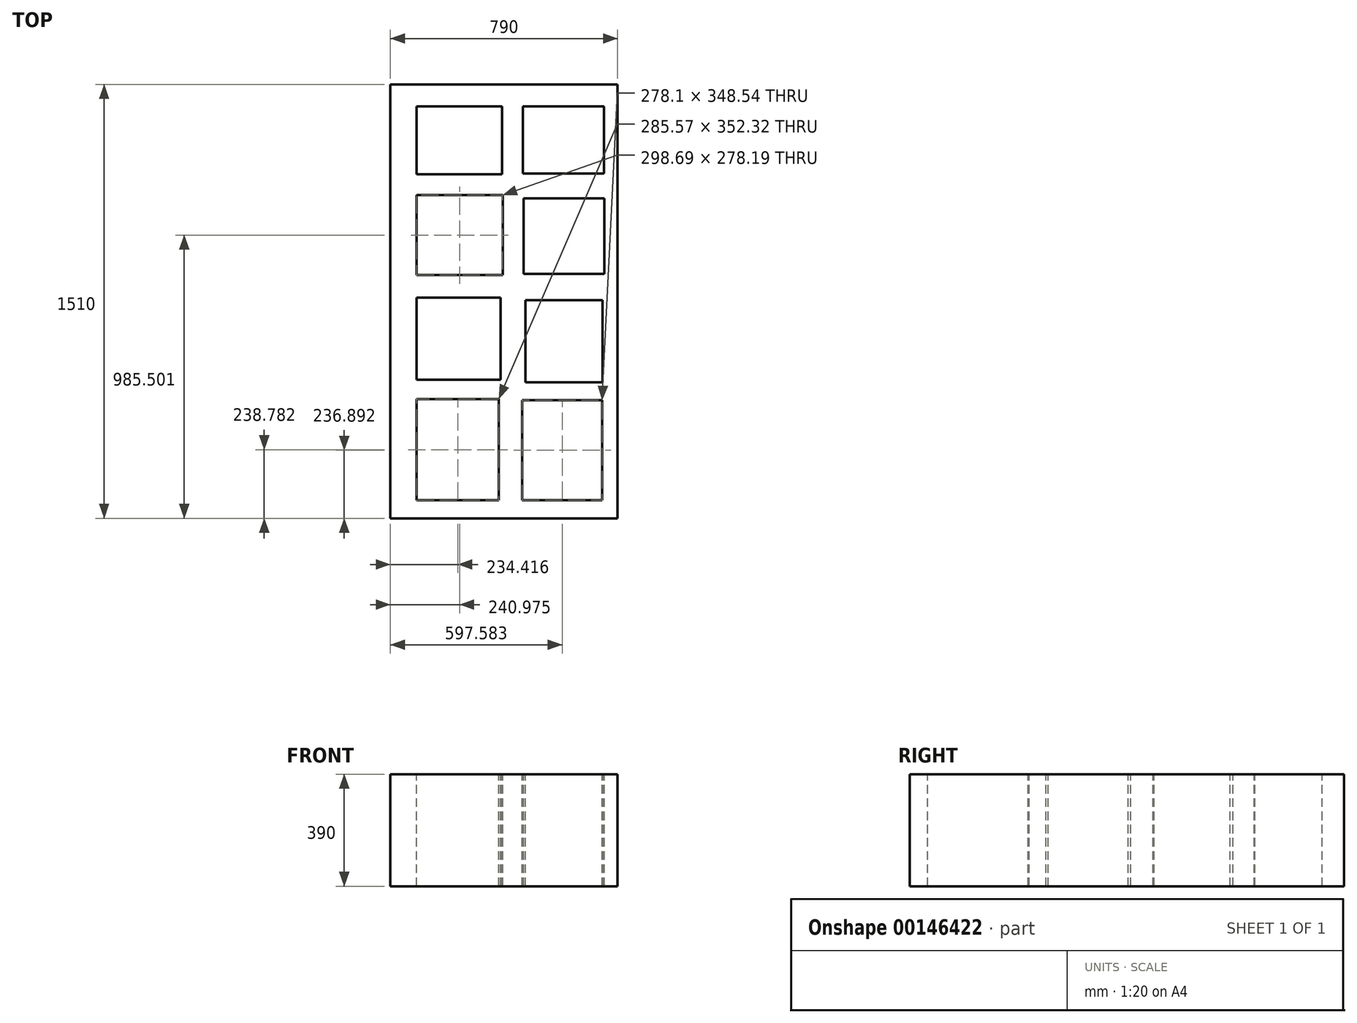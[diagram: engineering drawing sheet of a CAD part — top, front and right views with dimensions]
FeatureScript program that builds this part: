
annotation { "Feature Type Name" : "Feature", "Feature Type Description" : "" }
export const myFeature = defineFeature(function(context is Context, id is Id, definition is map)
    precondition{}
    {
        {
            var Q0;
            Q0=qCreatedBy(makeId("Top.planeOp"),FACE);
            var sketch = newSketch(context, id + "F0", { "sketchPlane" : qUnion([Q0])});
            skLineSegment(sketch, "E0.bottom", {"start": v(-91.63, -62.62) * mm, "end": v(698.37, -62.62) * mm});
            skLineSegment(sketch, "E0.top", {"start": v(-91.63, 1447.38) * mm, "end": v(698.37, 1447.38) * mm});
            skLineSegment(sketch, "E0.left", {"start": v(-91.63, -62.62) * mm, "end": v(-91.63, 1447.38) * mm});
            skLineSegment(sketch, "E0.right", {"start": v(698.37, -62.62) * mm, "end": v(698.37, 1447.38) * mm});
            skSolve(sketch);
        }
        {
            var Q0;
            Q0 = qSketchRegion(id + "F0", true);
            extrude(context, id + "F1", {"entities" : qUnion([Q0]), "depth" : 390 * mm});
        }
        {
            var Q0;
            Q0=makeQuery(id+"F1.opExtrude","CAP_FACE",FACE,{"disambiguationData":[OSD([sQuery(id+"F0.wireOp",EDGE,"E0.bottom"),sQuery(id+"F0.wireOp",EDGE,"E0.top"),sQuery(id+"F0.wireOp",EDGE,"E0.left"),sQuery(id+"F0.wireOp",EDGE,"E0.right")])],"isStart":false});
            var sketch = newSketch(context, id + "F2", { "sketchPlane" : qUnion([Q0])});
            skLineSegment(sketch, "E1.bottom", {"start": v(645, 0) * mm, "end": v(366.9, 0) * mm});
            skLineSegment(sketch, "E1.top", {"start": v(645, 348.54) * mm, "end": v(366.9, 348.54) * mm});
            skLineSegment(sketch, "E1.left", {"start": v(645, 0) * mm, "end": v(645, 348.54) * mm});
            skLineSegment(sketch, "E1.right", {"start": v(366.9, 0) * mm, "end": v(366.9, 348.54) * mm});
            skLineSegment(sketch, "E2.bottom", {"start": v(285.57, 0) * mm, "end": v(0, 0) * mm});
            skLineSegment(sketch, "E2.top", {"start": v(285.57, 352.32) * mm, "end": v(0, 352.32) * mm});
            skLineSegment(sketch, "E2.left", {"start": v(285.57, 0) * mm, "end": v(285.57, 352.32) * mm});
            skLineSegment(sketch, "E2.right", {"start": v(0, 0) * mm, "end": v(0, 352.32) * mm});
            skLineSegment(sketch, "E3.bottom", {"start": v(0, 419.3) * mm, "end": v(291.66, 419.3) * mm});
            skLineSegment(sketch, "E3.top", {"start": v(0, 705.66) * mm, "end": v(291.66, 705.66) * mm});
            skLineSegment(sketch, "E3.left", {"start": v(0, 419.3) * mm, "end": v(0, 705.66) * mm});
            skLineSegment(sketch, "E3.right", {"start": v(291.66, 419.3) * mm, "end": v(291.66, 705.66) * mm});
            skLineSegment(sketch, "E4.bottom", {"start": v(0, 783.78) * mm, "end": v(298.69, 783.78) * mm});
            skLineSegment(sketch, "E4.top", {"start": v(0, 1061.98) * mm, "end": v(298.69, 1061.98) * mm});
            skLineSegment(sketch, "E4.left", {"start": v(0, 783.78) * mm, "end": v(0, 1061.98) * mm});
            skLineSegment(sketch, "E4.right", {"start": v(298.69, 783.78) * mm, "end": v(298.69, 1061.98) * mm});
            skLineSegment(sketch, "E5.bottom", {"start": v(0, 1135.25) * mm, "end": v(296.63, 1135.25) * mm});
            skLineSegment(sketch, "E5.top", {"start": v(0, 1371.4) * mm, "end": v(296.63, 1371.4) * mm});
            skLineSegment(sketch, "E5.left", {"start": v(0, 1135.25) * mm, "end": v(0, 1371.4) * mm});
            skLineSegment(sketch, "E5.right", {"start": v(296.63, 1135.25) * mm, "end": v(296.63, 1371.4) * mm});
            skLineSegment(sketch, "E6.bottom", {"start": v(369.1, 1370.93) * mm, "end": v(650.8, 1370.93) * mm});
            skLineSegment(sketch, "E6.top", {"start": v(369.1, 1137.33) * mm, "end": v(650.8, 1137.33) * mm});
            skLineSegment(sketch, "E6.left", {"start": v(369.1, 1370.93) * mm, "end": v(369.1, 1137.33) * mm});
            skLineSegment(sketch, "E6.right", {"start": v(650.8, 1370.93) * mm, "end": v(650.8, 1137.33) * mm});
            skLineSegment(sketch, "E7.bottom", {"start": v(371.11, 1051.47) * mm, "end": v(652.63, 1051.47) * mm});
            skLineSegment(sketch, "E7.top", {"start": v(371.11, 787.74) * mm, "end": v(652.63, 787.74) * mm});
            skLineSegment(sketch, "E7.left", {"start": v(371.11, 1051.47) * mm, "end": v(371.11, 787.74) * mm});
            skLineSegment(sketch, "E7.right", {"start": v(652.63, 1051.47) * mm, "end": v(652.63, 787.74) * mm});
            skLineSegment(sketch, "E8.bottom", {"start": v(377.8, 696.7) * mm, "end": v(645.47, 696.7) * mm});
            skLineSegment(sketch, "E8.top", {"start": v(377.8, 411.34) * mm, "end": v(645.47, 411.34) * mm});
            skLineSegment(sketch, "E8.left", {"start": v(377.8, 696.7) * mm, "end": v(377.8, 411.34) * mm});
            skLineSegment(sketch, "E8.right", {"start": v(645.47, 696.7) * mm, "end": v(645.47, 411.34) * mm});
            skSolve(sketch);
        }
        {
            var Q0;
            Q0 = qSketchRegion(id + "F2", true);
            extrude(context, id + "F3", {"entities" : qUnion([Q0]), "operationType" : NewBodyOperationType.REMOVE, "endBound" : BoundingType.THROUGH_ALL, "oppositeDirection" : true, "depth" : 25 * mm});
        }
    });
